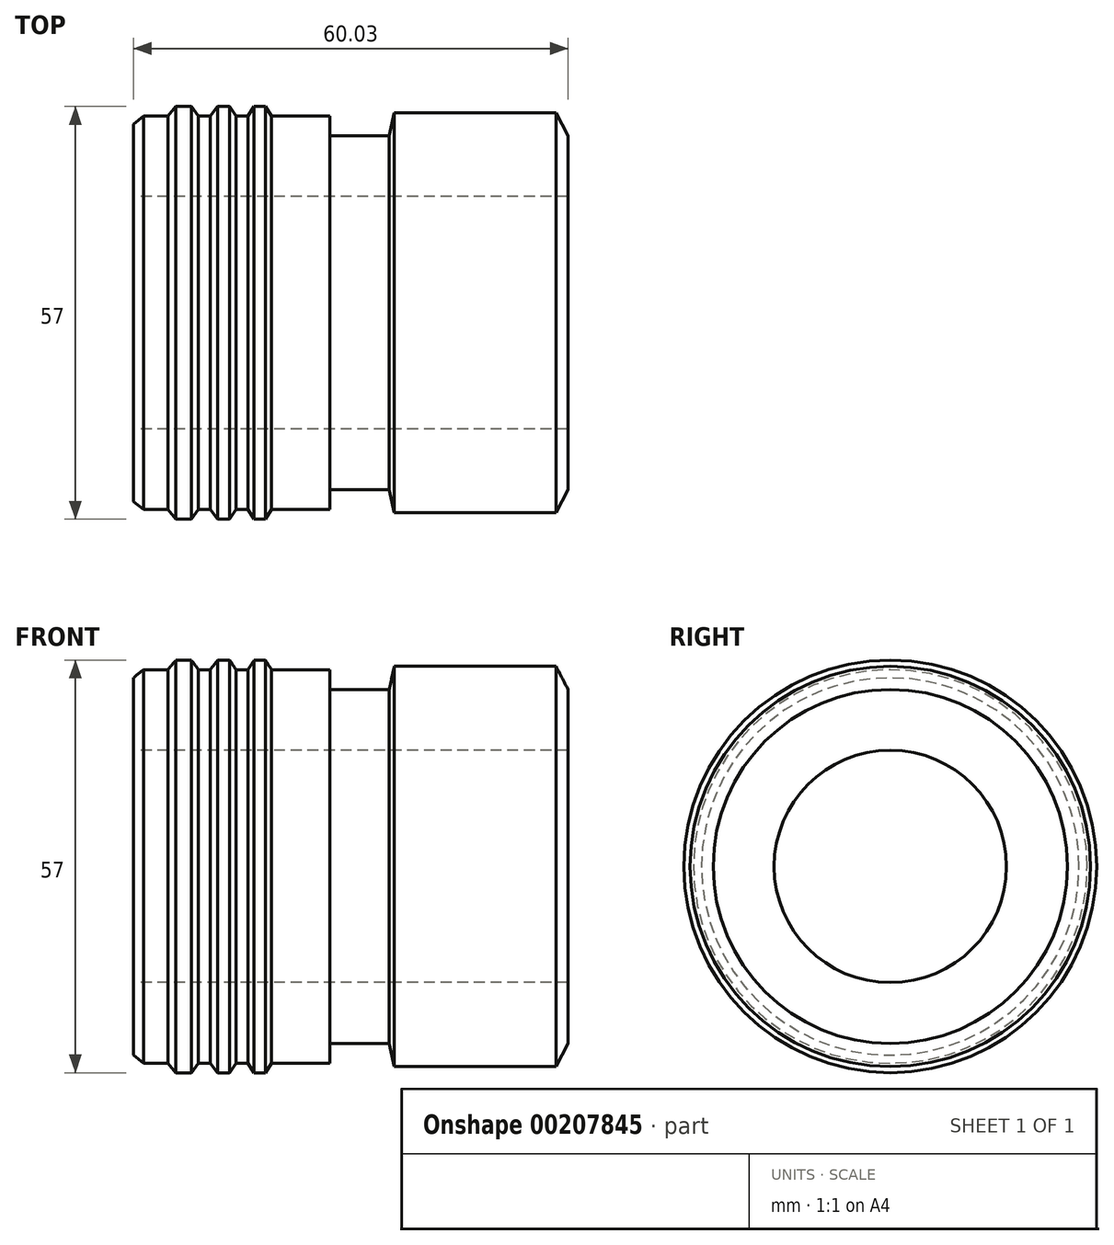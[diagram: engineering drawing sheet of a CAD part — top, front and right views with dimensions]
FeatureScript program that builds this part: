
annotation { "Feature Type Name" : "Feature", "Feature Type Description" : "" }
export const myFeature = defineFeature(function(context is Context, id is Id, definition is map)
    precondition{}
    {
        {
            var Q0;
            Q0=qCreatedBy(makeId("Front.planeOp"),FACE);
            var sketch = newSketch(context, id + "F0", { "sketchPlane" : qUnion([Q0])});
            skLineSegment(sketch, "E0", {"start": v(0, 0) * mm, "end": v(60, 0) * mm});
            skLineSegment(sketch, "E1", {"start": v(60.03, 16.04) * mm, "end": v(0, 16.04) * mm});
            skLineSegment(sketch, "E2", {"start": v(0, 16.04) * mm, "end": v(0, 26.07) * mm});
            skLineSegment(sketch, "E3", {"start": v(0, 26.07) * mm, "end": v(1.4, 27.19) * mm});
            skLineSegment(sketch, "E4", {"start": v(1.4, 27.19) * mm, "end": v(4.77, 27.19) * mm});
            skLineSegment(sketch, "E5", {"start": v(4.77, 27.19) * mm, "end": v(5.89, 28.5) * mm});
            skLineSegment(sketch, "E6", {"start": v(5.89, 28.5) * mm, "end": v(8, 28.5) * mm});
            skLineSegment(sketch, "E7", {"start": v(8, 28.5) * mm, "end": v(9, 27.19) * mm});
            skLineSegment(sketch, "E8", {"start": v(9, 27.19) * mm, "end": v(10.62, 27.19) * mm});
            skLineSegment(sketch, "E9", {"start": v(10.62, 27.19) * mm, "end": v(11.65, 28.5) * mm});
            skLineSegment(sketch, "E10", {"start": v(11.65, 28.5) * mm, "end": v(13.32, 28.5) * mm});
            skLineSegment(sketch, "E11", {"start": v(13.32, 28.5) * mm, "end": v(14.16, 27.19) * mm});
            skLineSegment(sketch, "E12", {"start": v(14.16, 27.19) * mm, "end": v(15.84, 27.19) * mm});
            skLineSegment(sketch, "E13", {"start": v(15.84, 27.19) * mm, "end": v(16.68, 28.5) * mm});
            skLineSegment(sketch, "E14", {"start": v(16.68, 28.5) * mm, "end": v(18.25, 28.5) * mm});
            skLineSegment(sketch, "E15", {"start": v(18.25, 28.5) * mm, "end": v(19.08, 27.19) * mm});
            skLineSegment(sketch, "E16", {"start": v(19.08, 27.19) * mm, "end": v(27.15, 27.19) * mm});
            skLineSegment(sketch, "E17", {"start": v(27.15, 27.19) * mm, "end": v(27.15, 24.46) * mm});
            skLineSegment(sketch, "E18", {"start": v(27.15, 24.46) * mm, "end": v(35.35, 24.46) * mm});
            skLineSegment(sketch, "E19", {"start": v(35.35, 24.46) * mm, "end": v(36.03, 27.65) * mm});
            skLineSegment(sketch, "E20", {"start": v(36.03, 27.65) * mm, "end": v(58.37, 27.65) * mm});
            skLineSegment(sketch, "E21", {"start": v(58.37, 27.65) * mm, "end": v(60.03, 24.46) * mm});
            skLineSegment(sketch, "E22", {"start": v(78.75, 0) * mm, "end": v(78.75, 16.7) * mm});
            skLineSegment(sketch, "E23", {"start": v(60.03, 24.46) * mm, "end": v(60.03, 16.04) * mm});
            skSolve(sketch);
        }
        {
            var Q0;
            Q0 = qSketchRegion(id + "F0", true);
            var Q1;
            Q1=sQuery(id+"F0.wireOp",EDGE,"E0");
            revolve(context, id + "F1", {"entities" : qUnion([Q0]), "axis" : qUnion([Q1]), "revolveType" : RevolveType.FULL});
        }
    });
